# Revit family: 75024XXX_NEW
name_source: partatom
category: Plumbing Fixtures
revit_build: Autodesk Revit 2018 (Build: 20170223_1515(x64)
units: mm (PartAtom-declared; Revit-internal decimal feet)

## family parameters
Always vertical = No
Cut with Voids When Loaded = No
Part Type = Normal
Room Calculation Point = No
Round Connector Dimension = Use Diameter
Shared = No
Work Plane-Based = Yes

## types (3) — shared parameters
Always visible = Yes
BIMobject category = Wash Basins
Default Elevation = 1219.2 mm  [stored 4 ft]
Design country = Germany
Edition number = 1
IFC Classification = Sanitary Terminal
Installation instructions = https://www.hansgrohe.com
Manufacturer country = Germany
Manufacturer name = hansgrohe
NBS Reference Code = 31-75
NBS Reference Description = Sanitary Accessories
Product Guid = 2624544d-6d0f-46c9-9171-ee2c5957058f
Product SKU = 75024XXX
Product data url = https://www.bimobject.com
Product family = Vivenis
Product group = Basin mixers
Product name = 75024XXX Vivenis Single lever basin mixer 110 CoolStart without waste set
Product url = https://www.hansgrohe.com
QR code = https://www.bimobject.com
Technical description = https://www.hansgrohe.com
UNSPSC Code = 301815
Weight Net (Kg) = 1,4

## per-type parameters (varying)
| type | Material 1 |
| 700 Matt White | Hansgrohe - Vivenis - 700 Matt White |
| 670 Matte Black | Hansgrohe - Vivenis - 670 Matte Black |
| 000 Chrome | Hansgrohe - Vivenis - 000 Chrome |

note: [stored X ft] marks values corroborated as IEEE doubles in the binary element streams (Revit-internal decimal feet)

## geometry (parser evidence)
native form markers: Sweep x2
no freeform markers — native parametric forms only
